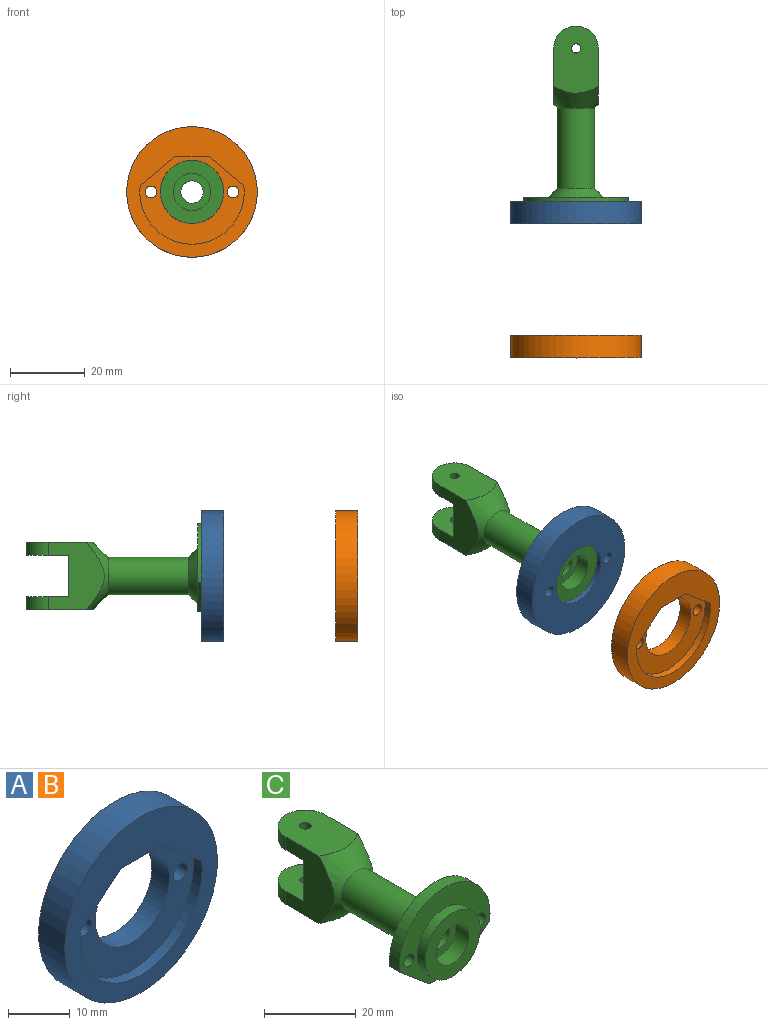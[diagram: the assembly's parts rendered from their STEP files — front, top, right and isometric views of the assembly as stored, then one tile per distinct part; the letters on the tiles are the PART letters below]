
ASSEMBLY  parts=3 mates=2
PART A: 11 faces, bbox 35x6x35 mm
  f0: cylinder r=1.6mm len=4mm, axis (0,-1,0), area 40.2mm2, adj f4,f5
  f1: cylinder r=1.6mm len=4mm, axis (0,-1,0), area 40.2mm2, adj f4,f5
  f2: cylinder r=8.5mm len=17mm, axis (0,-1,0), area 213.6mm2, adj f4,f5
  f3: cylinder r=17.5mm len=35mm, axis (0,-1,0), area 659.7mm2, adj f4,f10
  f4: plane 35x35mm, normal (0,1,0), area 719mm2, adj f0,f1,f2,f3
  f5: plane 28x23.5mm, normal (0,-1,0), area 256.5mm2, adj f0,f1,f2,f6,f7,f8,f9
  f6: cylinder r=14mm len=28mm, axis (0,1,0), area 94.8mm2, adj f5,f7,f9,f10
  f7: plane 9.3x7.8mm, normal (0.64,0,-0.77), area 24.3mm2, adj f5,f6,f8,f10
  f8: plane 9.19x2mm, normal (0,0,-1), area 18.4mm2, adj f5,f7,f9,f10
  f9: plane 9.3x7.8mm, normal (-0.64,0,-0.77), area 24.3mm2, adj f5,f6,f8,f10
  f10: plane 35x35mm, normal (0,-1,0), area 462.6mm2, adj f3,f6,f7,f8,f9
PART B: same geometry as A
PART C: 30 faces, bbox 28x51.5x25.7 mm
  f0: cylinder r=1.6mm len=3.2mm, axis (0,-1,0), area 30.2mm2, adj f5,f6
  f1: plane 9.19x3mm, normal (0,0,-1), area 27.6mm2, adj f2,f3,f5,f6
  f2: plane 9.3x7.8mm, normal (0.64,0,-0.77), area 36.4mm2, adj f1,f5,f6,f8
  f3: plane 9.3x7.8mm, normal (-0.64,0,-0.77), area 36.4mm2, adj f1,f5,f6,f8
  f4: cylinder r=1.6mm len=3.2mm, axis (0,-1,0), area 30.2mm2, adj f5,f6
  f5: plane 28x23.5mm, normal (0,1,0), area 306.8mm2, adj f0,f1,f2,f3,f4,f7,f8
  f6: plane 28x23.5mm, normal (0,-1,0), area 256.5mm2, adj f0,f1,f2,f3,f4,f8,f9
  f7: cone r=6.25mm half-angle=45deg, axis (0,-1,0), area 138.8mm2, adj f5,f13
  f8: cylinder r=14mm len=28mm, axis (0,-1,0), area 142.1mm2, adj f2,f3,f5,f6
  f9: cylinder r=8.5mm len=17mm, axis (0,-1,0), area 133.5mm2, adj f6,f10
  f10: plane 17x17mm, normal (0,-1,0), area 148.4mm2, adj f9,f11
  f11: cylinder r=5mm len=10mm, axis (0,-1,0), area 125.7mm2, adj f10,f12
  f12: plane 10x10mm, normal (0,-1,0), area 50.3mm2, adj f11,f27
  f13: cylinder r=5mm len=21.5mm, axis (0,-1,0), area 675.4mm2, adj f7,f14
  f14: cone r=11mm half-angle=45deg, axis (0,1,0), area 194.4mm2, adj f13,f15,f16,f19,f20
  f15: plane 23.44x17.72mm, normal (-1,0,0), area 177.1mm2, adj f14,f16,f17,f18,f20,f21,f22,f24
  f16: plane 18.25x12.49mm, normal (0,0,1), area 188.1mm2, adj f14,f15,f17,f19,f28
  f17: cylinder r=6mm len=12mm, axis (0,0,1), area 66mm2, adj f15,f16,f19,f24
  f18: cylinder r=6mm len=12mm, axis (0,0,1), area 66mm2, adj f15,f19,f20,f21
  f19: plane 23.44x17.72mm, normal (1,0,0), area 177.1mm2, adj f14,f16,f17,f18,f20,f21,f23,f24
  f20: plane 18.8x13.59mm, normal (0,0,-1), area 188.1mm2, adj f14,f15,f18,f19,f29
  f21: plane 12x11.5mm, normal (0,0,1), area 117.6mm2, adj f15,f18,f19,f22,f23,f29
  f22: plane 11x6mm, normal (0,1,0), area 18.5mm2, adj f15,f21,f24,f25
  f23: plane 11x6mm, normal (0,1,0), area 18.5mm2, adj f19,f21,f24,f25
  f24: plane 12x11.5mm, normal (0,0,-1), area 117.6mm2, adj f15,f17,f19,f22,f23,f28
  f25: cylinder r=5.5mm len=11mm, axis (0,-1,0), area 241.9mm2, adj f22,f23,f26
  f26: plane 11x11mm, normal (0,1,0), area 66.8mm2, adj f25,f27
  f27: cylinder r=3mm len=29mm, axis (0,-1,0), area 546.6mm2, adj f12,f26
  f28: cylinder r=1.25mm len=3.5mm, axis (0,0,-1), area 27.5mm2, adj f16,f24
  f29: cylinder r=1.25mm len=3.5mm, axis (0,0,-1), area 27.5mm2, adj f20,f21
PLACE A rot(axis=(1,0,0),180deg) t=(22.32,62.84,-2.48)mm
PLACE B t=(22.32,24.84,-2.48)mm
PLACE C t=(22.32,111.84,-2.48)mm
MATE fastened A.f2 <-> B.f3  axis (0,-1,0) through (22.32,58.84,-2.48)mm
MATE fastened C.f7 <-> A.f2  axis (0,-1,0) through (22.32,62.84,-2.48)mm
